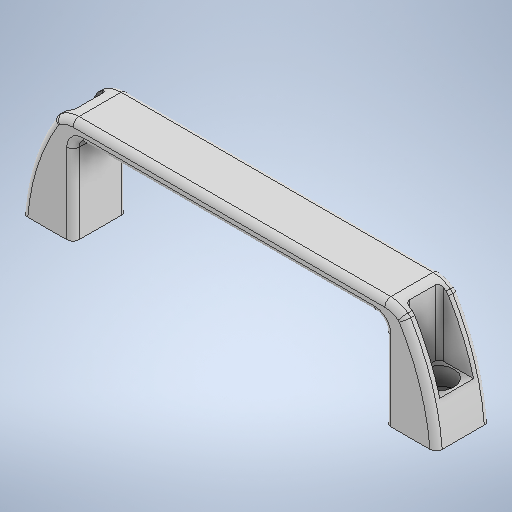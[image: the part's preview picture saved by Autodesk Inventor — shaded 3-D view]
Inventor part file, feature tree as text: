
AUTODESK INVENTOR PART (.ipt)
format: ipt  version: 2025 (Build 290162000, 162)  size: 340,480 bytes
history: native  units: mm
features: sketch x3, extrude x2, fillet x2, hole x1, mirror x1
ambient origin geometry x8: Origin, YZ Plane, XZ Plane, XY Plane, X Axis, Y Axis, Z Axis, Center Point
bodies: Solid1 (feature_tree)
feature tree (9):
  extrude  "Extrusion1"  Depth=8.0mm
  fillet  "Fillet1"  Radius=5.0mm
  fillet  "Fillet2"  Radius=152.0mm
  extrude  "Extrusion2"  Depth=3.0mm
  hole  "Hole1"  [1 undecoded]
  mirror  "Mirror1"
  sketch  "Sketch1"  dims[d1=44.0mm d2=8.0mm d4=5.0mm d5=152.0mm]
  sketch  "Sketch2"  dims[d6=26.5mm d7=0.0mm d8=3.0mm]
  sketch  "Sketch3"  dims[d9=3.0mm d10=5.0mm d11=5.0mm d12=5.0mm d13=5.0mm d14=2.0mm d15=5.0mm d16=2.0mm d17=33.0mm d18=0.0mm d19=8.0mm d20=6.0mm d21=15.0mm d22=8.6mm d23=90.0deg d24=8.0mm d25=20.594885mm d27=89.15mm]
note: 1 required parameter value undecoded (feature->parameter linkage not recoverable at this tier; creation-order binding heuristic only, values carry confidence <= 0.55)
